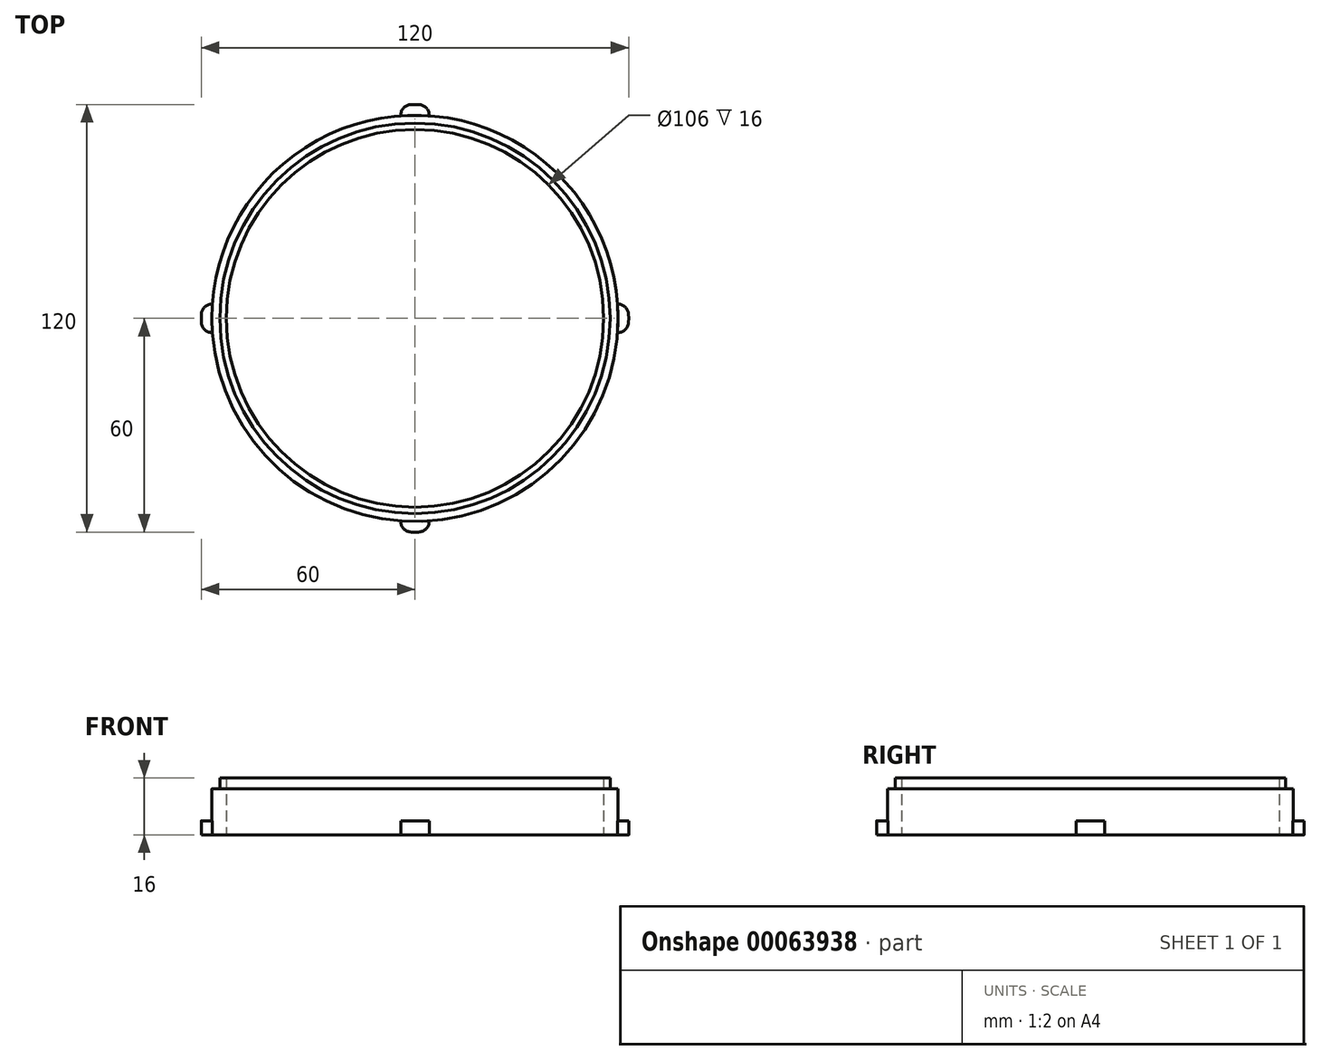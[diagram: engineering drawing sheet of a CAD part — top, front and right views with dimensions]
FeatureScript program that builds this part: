
annotation { "Feature Type Name" : "Feature", "Feature Type Description" : "" }
export const myFeature = defineFeature(function(context is Context, id is Id, definition is map)
    precondition{}
    {
        {
            var Q0;
            Q0=qCreatedBy(makeId("Top.planeOp"),FACE);
            var sketch = newSketch(context, id + "F0", { "sketchPlane" : qUnion([Q0])});
            skCircle(sketch, "E0", {"center": v(0, 0) * mm, "radius": 57 * mm});
            skCircle(sketch, "E1", {"center": v(0, 0) * mm, "radius": 53 * mm});
            skSolve(sketch);
        }
        {
            var Q0;
            Q0=makeQuery(id+"F0.imprint","IMPRINT",FACE,{"disambiguationData":[TD([[makeQuery(id+"F0.imprint","IMPRINT",EDGE,{"derivedFrom":sQuery(id+"F0.wireOp",EDGE,"E0")}),1.0]])]});
            extrude(context, id + "F1", {"entities" : qUnion([Q0]), "depth" : 13 * mm});
        }
        {
            var Q0;
            Q0=qCreatedBy(makeId("Top.planeOp"),FACE);
            var sketch = newSketch(context, id + "F2", { "sketchPlane" : qUnion([Q0])});
            skArc(sketch, "E2", {"start": v(-59.87, 4) * mm, "mid": v(-60, 0) * mm, "end": v(-59.87, -4) * mm});
            skArc(sketch, "E3.0", {"start": v(-56.86, 4) * mm, "mid": v(-57, 0) * mm, "end": v(-56.86, -4) * mm});
            skLineSegment(sketch, "E4", {"start": v(-59.87, 4) * mm, "end": v(-56.86, 4) * mm});
            skLineSegment(sketch, "E5", {"start": v(-59.87, -4) * mm, "end": v(-56.86, -4) * mm});
            skLineSegment(sketch, "E6", {"start": v(59.87, -4) * mm, "end": v(56.86, -4) * mm});
            skLineSegment(sketch, "E7", {"start": v(59.87, 4) * mm, "end": v(56.86, 4) * mm});
            skLineSegment(sketch, "E8", {"start": v(4, -59.87) * mm, "end": v(4, -56.86) * mm});
            skLineSegment(sketch, "E9", {"start": v(-4, -59.87) * mm, "end": v(-4, -56.86) * mm});
            skLineSegment(sketch, "E10", {"start": v(-4, 59.87) * mm, "end": v(-4, 56.86) * mm});
            skLineSegment(sketch, "E11", {"start": v(4, 59.87) * mm, "end": v(4, 56.86) * mm});
            skArc(sketch, "E12.trimOffspring", {"start": v(4, 59.87) * mm, "mid": v(0, 60) * mm, "end": v(-4, 59.87) * mm});
            skArc(sketch, "E13.trimOffspring", {"start": v(4, 56.86) * mm, "mid": v(0, 57) * mm, "end": v(-4, 56.86) * mm});
            skArc(sketch, "E14.trimOffspring", {"start": v(59.87, -4) * mm, "mid": v(60, 0) * mm, "end": v(59.87, 4) * mm});
            skArc(sketch, "E15.trimOffspring", {"start": v(-4, -59.87) * mm, "mid": v(0, -60) * mm, "end": v(4, -59.87) * mm});
            skArc(sketch, "E16.trimOffspring", {"start": v(-4, -56.86) * mm, "mid": v(0, -57) * mm, "end": v(4, -56.86) * mm});
            skArc(sketch, "E17.0", {"start": v(56.86, -4) * mm, "mid": v(57, 0) * mm, "end": v(56.86, 4) * mm});
            skSolve(sketch);
        }
        {
            var Q0;
            Q0=makeQuery(id+"F2.imprint","IMPRINT",FACE,{"disambiguationData":[TD([[makeQuery(id+"F2.imprint","IMPRINT",EDGE,{"derivedFrom":sQuery(id+"F2.wireOp",EDGE,"E2")}),1.0]])]});
            var Q1;
            Q1=makeQuery(id+"F2.imprint","IMPRINT",FACE,{"disambiguationData":[TD([[makeQuery(id+"F2.imprint","IMPRINT",EDGE,{"derivedFrom":sQuery(id+"F2.wireOp",EDGE,"E10")}),1.0]])]});
            var Q2;
            Q2=makeQuery(id+"F2.imprint","IMPRINT",FACE,{"disambiguationData":[TD([[makeQuery(id+"F2.imprint","IMPRINT",EDGE,{"derivedFrom":sQuery(id+"F2.wireOp",EDGE,"E8")}),1.0]])]});
            var Q3;
            Q3=makeQuery(id+"F2.imprint","IMPRINT",FACE,{"disambiguationData":[TD([[makeQuery(id+"F2.imprint","IMPRINT",EDGE,{"derivedFrom":sQuery(id+"F2.wireOp",EDGE,"E6")}),-1.0]])]});
            extrude(context, id + "F3", {"entities" : qUnion([Q0, Q1, Q2, Q3]), "operationType" : NewBodyOperationType.ADD, "depth" : 4 * mm});
        }
        {
            var Q0;
            Q0=makeQuery(id+"F3.opExtrude","SWEPT_EDGE",EDGE,{"disambiguationData":[OSD([sQuery(id+"F2.wireOp",EDGE,"E6"),sQuery(id+"F2.wireOp",EDGE,"E14.trimOffspring")])]});
            var Q1;
            Q1=makeQuery(id+"F3.opExtrude","SWEPT_EDGE",EDGE,{"disambiguationData":[OSD([sQuery(id+"F2.wireOp",EDGE,"E7"),sQuery(id+"F2.wireOp",EDGE,"E14.trimOffspring")])]});
            var Q2;
            Q2=makeQuery(id+"F3.opExtrude","SWEPT_EDGE",EDGE,{"disambiguationData":[OSD([sQuery(id+"F2.wireOp",EDGE,"E9"),sQuery(id+"F2.wireOp",EDGE,"E15.trimOffspring")])]});
            var Q3;
            Q3=makeQuery(id+"F3.opExtrude","SWEPT_EDGE",EDGE,{"disambiguationData":[OSD([sQuery(id+"F2.wireOp",EDGE,"E8"),sQuery(id+"F2.wireOp",EDGE,"E15.trimOffspring")])]});
            var Q4;
            Q4=makeQuery(id+"F3.opExtrude","SWEPT_EDGE",EDGE,{"disambiguationData":[OSD([sQuery(id+"F2.wireOp",EDGE,"E2"),sQuery(id+"F2.wireOp",EDGE,"E5")])]});
            var Q5;
            Q5=makeQuery(id+"F3.opExtrude","SWEPT_EDGE",EDGE,{"disambiguationData":[OSD([sQuery(id+"F2.wireOp",EDGE,"E2"),sQuery(id+"F2.wireOp",EDGE,"E4")])]});
            var Q6;
            Q6=makeQuery(id+"F3.opExtrude","SWEPT_EDGE",EDGE,{"disambiguationData":[OSD([sQuery(id+"F2.wireOp",EDGE,"E10"),sQuery(id+"F2.wireOp",EDGE,"E12.trimOffspring")])]});
            var Q7;
            Q7=makeQuery(id+"F3.opExtrude","SWEPT_EDGE",EDGE,{"disambiguationData":[OSD([sQuery(id+"F2.wireOp",EDGE,"E11"),sQuery(id+"F2.wireOp",EDGE,"E12.trimOffspring")])]});
            fillet(context, id + "F4", {"entities" : qUnion([Q0, Q1, Q2, Q3, Q4, Q5, Q6, Q7]), "radius" : 3 * mm, "tangentPropagation" : true, "allowEdgeOverflow" : false});
        }
        {
            var Q0;
            Q0=makeQuery(id+"F1.opExtrude","CAP_FACE",FACE,{"disambiguationData":[OSD([sQuery(id+"F0.wireOp",EDGE,"E0"),sQuery(id+"F0.wireOp",EDGE,"E1")])],"isStart":false});
            var sketch = newSketch(context, id + "F5", { "sketchPlane" : qUnion([Q0])});
            skCircle(sketch, "E18", {"center": v(0, 0) * mm, "radius": 54.8 * mm});
            skSolve(sketch);
        }
        {
            var Q0;
            Q0=makeQuery(id+"F5.imprint","IMPRINT",FACE,{"disambiguationData":[TD([[makeQuery(id+"F5.imprint","IMPRINT",EDGE,{"derivedFrom":sQuery(id+"F5.wireOp",EDGE,"E18")}),1.0]])]});
            extrude(context, id + "F6", {"entities" : qUnion([Q0]), "operationType" : NewBodyOperationType.ADD, "depth" : 3 * mm});
        }
    });
